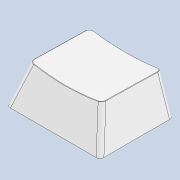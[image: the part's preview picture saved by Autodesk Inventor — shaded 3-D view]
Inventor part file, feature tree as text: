
AUTODESK INVENTOR PART (.ipt)
format: ipt  version: 2021 (Build 250183000, 183)  size: 240,128 bytes
history: native  units: in
note: dims shown in document units (in); Inventor stores cm internally (conversion verified against a paired STEP export)
features: chamfer x1
ambient origin geometry x8: Origin, YZ Plane, XZ Plane, XY Plane, X Axis, Y Axis, Z Axis, Center Point
bodies: Solid1 (feature_tree)
feature tree (1):
  chamfer  "Chamfer1"  [1 undecoded]
note: 1 required parameter value undecoded (feature->parameter linkage not recoverable at this tier; creation-order binding heuristic only, values carry confidence <= 0.55)
